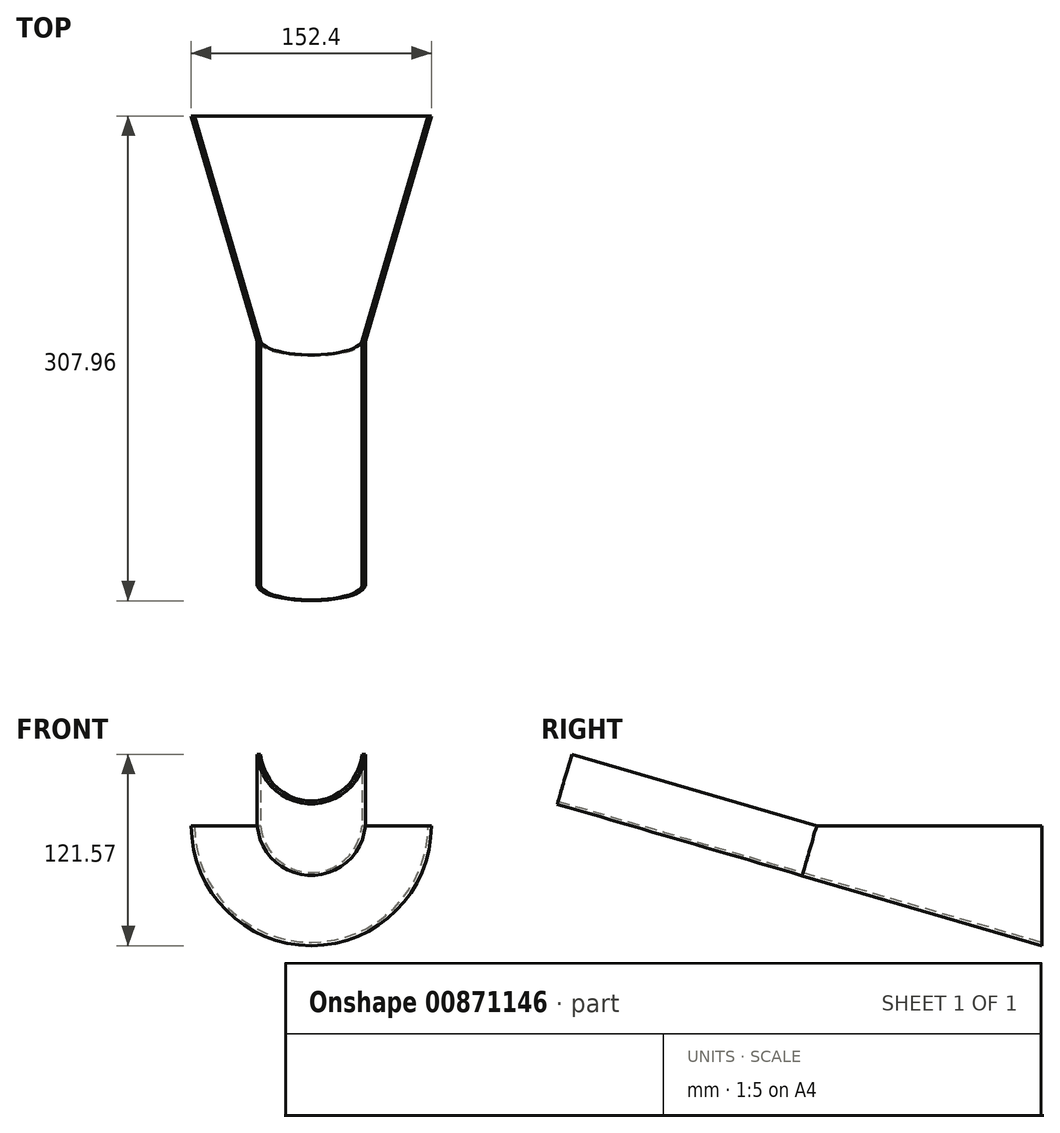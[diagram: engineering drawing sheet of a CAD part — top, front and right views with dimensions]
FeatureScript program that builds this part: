
annotation { "Feature Type Name" : "Feature", "Feature Type Description" : "" }
export const myFeature = defineFeature(function(context is Context, id is Id, definition is map)
    precondition{}
    {
        {
            var Q0;
            Q0=qCreatedBy(makeId("Top.planeOp"),FACE);
            var sketch = newSketch(context, id + "F0", { "sketchPlane" : qUnion([Q0])});
            skLineSegment(sketch, "E0", {"start": v(0, 0) * mm, "end": v(-29.67, 0) * mm});
            skLineSegment(sketch, "E1", {"start": v(-29.67, 0) * mm, "end": v(-74.12, 152.4) * mm});
            skLineSegment(sketch, "E2", {"start": v(0, 152.4) * mm, "end": v(0, 0) * mm});
            skLineSegment(sketch, "E3", {"start": v(0, 152.4) * mm, "end": v(-74.12, 152.4) * mm});
            skLineSegment(sketch, "E4", {"start": v(-31.75, 0) * mm, "end": v(-76.2, 152.4) * mm});
            skLineSegment(sketch, "E5", {"start": v(-29.67, 0) * mm, "end": v(-29.67, -5) * mm});
            skLineSegment(sketch, "E6", {"start": v(-76.2, 152.4) * mm, "end": v(-74.12, 152.4) * mm});
            skLineSegment(sketch, "E7", {"start": v(-31.75, 0) * mm, "end": v(-29.67, 0) * mm});
            skSolve(sketch);
        }
        {
            var Q0;
            {var subQ0=sQuery(id+"F0.wireOp",EDGE,"E1");Q0=makeQuery(id+"F0.imprint","IMPRINT",FACE,{"disambiguationData":[TD([[makeQuery(id+"F0.imprint","IMPRINT",EDGE,{"derivedFrom":subQ0}),1.0]])]});}
            var Q1;
            {var subQ0=sQuery(id+"F0.wireOp",EDGE,"E5");Q1=makeQuery(id+"F0.imprint","IMPRINT",FACE,{"disambiguationData":[TD([[makeQuery(id+"F0.imprint","IMPRINT",EDGE,{"derivedFrom":subQ0}),1.0]])]});}
            var Q2;
            Q2=sQuery(id+"F0.wireOp",EDGE,"E2");
            revolve(context, id + "F1", {"surfaceOperationType" : NewSurfaceOperationType.NEW, "entities" : qUnion([Q0, Q1]), "axis" : qUnion([Q2]), "revolveType" : RevolveType.ONE_DIRECTION, "angle" : 180 * degree});
        }
        {
            var Q0;
            Q0=qCreatedBy(makeId("Right.planeOp"),FACE);
            var sketch = newSketch(context, id + "F2", { "sketchPlane" : qUnion([Q0])});
            skLineSegment(sketch, "E8", {"start": v(0, 0) * mm, "end": v(0, -31.75) * mm});
            skLineSegment(sketch, "E9", {"start": v(0, -31.75) * mm, "end": v(152.4, -76.2) * mm});
            skLineSegment(sketch, "E10", {"start": v(0, -31.75) * mm, "end": v(9.26, 0) * mm});
            skLineSegment(sketch, "E11", {"start": v(9.26, 0) * mm, "end": v(0, 2.7) * mm});
            skLineSegment(sketch, "E12", {"start": v(0, 2.7) * mm, "end": v(-9.26, -29.05) * mm});
            skLineSegment(sketch, "E13", {"start": v(-9.26, -29.05) * mm, "end": v(0, -31.75) * mm});
            skSolve(sketch);
        }
        {
            var Q0;
            Q0=makeQuery(id+"F2.imprint","IMPRINT",FACE,{"disambiguationData":[TD([[makeQuery(id+"F2.imprint","IMPRINT",EDGE,{"derivedFrom":sQuery(id+"F2.wireOp",EDGE,"E10")}),1.0]])]});
            extrude(context, id + "F3", {"entities" : qUnion([Q0]), "operationType" : NewBodyOperationType.ADD, "depth" : 44.6 * mm, "offsetDistance" : 25 * mm, "hasSecondDirection" : true, "secondDirectionOppositeDirection" : true, "secondDirectionDepth" : 39.8 * mm});
        }
        {
            var Q0;
            {var subQ0=sQuery(id+"F2.wireOp",EDGE,"E13");var subQ1=sQuery(id+"F2.wireOp",EDGE,"E11");var subQ2=sQuery(id+"F2.wireOp",EDGE,"E10");var subQ4=makeQuery(id+"F3.opExtrude","SWEPT_FACE",FACE,{"disambiguationData":[OSD([subQ2])]});Q0=makeQuery(id+"F3.boolean.opBoolean","SPLIT",FACE,{"disambiguationData":[TD([makeQuery(id+"F3.opExtrude","CAP_FACE",FACE,{"disambiguationData":[OSD([subQ2,subQ1,sQuery(id+"F2.wireOp",EDGE,"E12"),subQ0])],"isStart":false})])],"derivedFrom":subQ4});}
            var Q1;
            {var subQ0=sQuery(id+"F2.wireOp",EDGE,"E13");var subQ1=sQuery(id+"F2.wireOp",EDGE,"E11");var subQ2=sQuery(id+"F2.wireOp",EDGE,"E10");var subQ3=makeQuery(id+"F3.opExtrude","SWEPT_FACE",FACE,{"disambiguationData":[OSD([subQ2])]});Q1=makeQuery(id+"F3.boolean.opBoolean","SPLIT",FACE,{"disambiguationData":[TD([makeQuery(id+"F3.opExtrude","CAP_FACE",FACE,{"disambiguationData":[OSD([subQ2,subQ1,sQuery(id+"F2.wireOp",EDGE,"E12"),subQ0])],"isStart":true})])],"derivedFrom":subQ3});}
            extrude(context, id + "F4", {"entities" : qUnion([Q0, Q1]), "operationType" : NewBodyOperationType.REMOVE, "oppositeDirection" : true, "depth" : 25 * mm, "offsetDistance" : 25 * mm});
        }
        {
            var Q0;
            {var subQ0=sQuery(id+"F0.wireOp",EDGE,"E1");Q0=makeQuery(id+"F3.boolean.opBoolean","SPLIT",FACE,{"disambiguationData":[TD([makeQuery(id+"F1.opRevolve","SWEPT_FACE",FACE,{"disambiguationData":[OSD([subQ0])]})])],"derivedFrom":makeQuery(id+"F3.opExtrude","SWEPT_FACE",FACE,{"disambiguationData":[OSD([sQuery(id+"F2.wireOp",EDGE,"E10")])]})});}
            extrude(context, id + "F5", {"entities" : qUnion([Q0]), "operationType" : NewBodyOperationType.REMOVE, "oppositeDirection" : true, "depth" : 25 * mm, "offsetDistance" : 25 * mm});
        }
        {
            var Q0;
            Q0=makeQuery(id+"F3.opExtrude","SWEPT_FACE",FACE,{"disambiguationData":[OSD([sQuery(id+"F2.wireOp",EDGE,"E12")])]});
            extrude(context, id + "F6", {"entities" : qUnion([Q0]), "operationType" : NewBodyOperationType.ADD, "depth" : 152.4 * mm, "offsetDistance" : 25 * mm});
        }
    });
